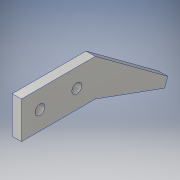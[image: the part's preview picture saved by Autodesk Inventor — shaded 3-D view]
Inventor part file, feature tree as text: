
AUTODESK INVENTOR PART (.ipt)
format: ipt  version: 2016 (Build 200138000, 138)  size: 107,008 bytes
history: native  units: in
note: dims shown in document units (in); Inventor stores cm internally (conversion verified against a paired STEP export)
features: extrude x1, sketch x1
ambient origin geometry x8: Origin, YZ Plane, XZ Plane, XY Plane, X Axis, Y Axis, Z Axis, Center Point
bodies: Solid1 (feature_tree)
feature tree (2):
  extrude  "Extrusion1"  Depth=0.25in
  sketch  "Sketch1"  dims[d0=2.0in d4=1.0994in d5=2.0in d6=0.25in d7=1.0in d8=0.2656in d9=0.2656in d10=0.5in d11=1.5in d12=0.5in d13=0.5in d14=0.25in d15=0.0in]
